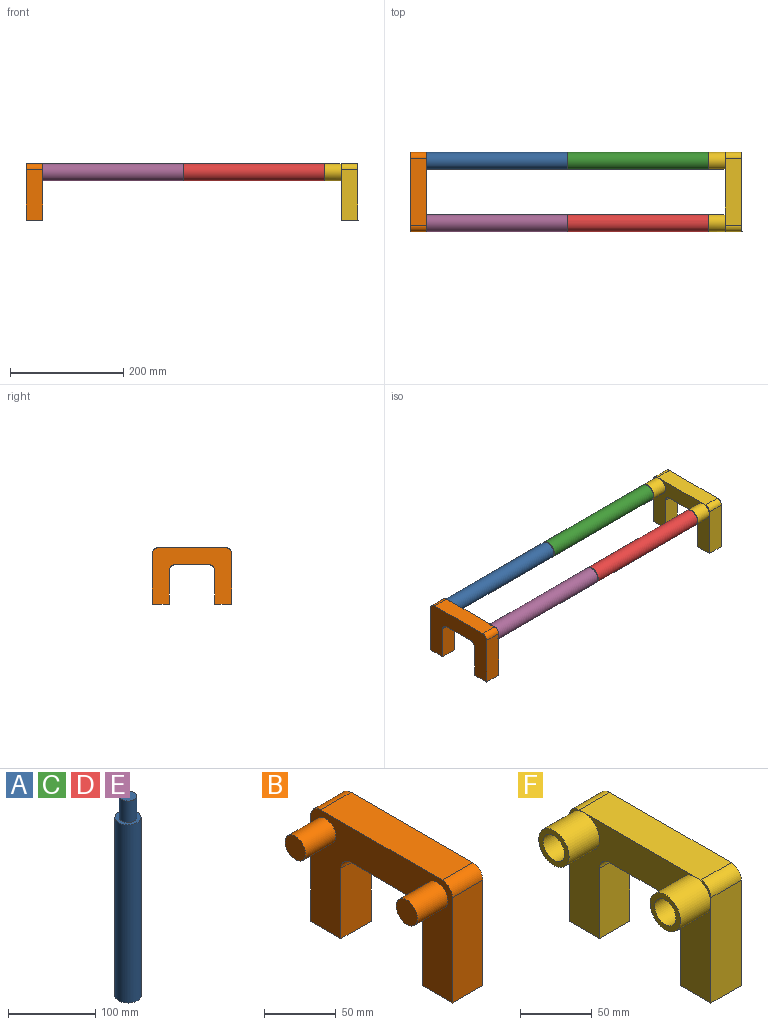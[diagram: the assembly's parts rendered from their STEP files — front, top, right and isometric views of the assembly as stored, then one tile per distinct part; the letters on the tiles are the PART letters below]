
ASSEMBLY  parts=6 mates=5
PART A: 7 faces, bbox 30x30x280 mm
  f0: cylinder r=15mm len=250mm, axis (0,0,-1), area 23561.9mm2, adj f1,f2
  f1: plane 30x30mm, normal (0,0,1), area 392.7mm2, adj f0,f3
  f2: plane 30x30mm, normal (0,0,-1), area 360.5mm2, adj f0,f5
  f3: cylinder r=10mm len=30mm, axis (0,0,-1), area 1885mm2, adj f1,f4
  f4: plane 20x20mm, normal (0,0,1), area 314.2mm2, adj f3
  f5: cylinder r=10.5mm len=31mm, axis (0,0,-1), area 2045.2mm2, adj f2,f6
  f6: plane 21x21mm, normal (0,0,-1), area 346.4mm2, adj f5
PART B: 18 faces, bbox 60x140x100 mm
  f0: plane 60x30mm, normal (0,1,0), area 1800mm2, adj f1,f3,f5,f16
  f1: plane 140x100mm, normal (-1,0,0), area 7739.5mm2, adj f0,f2,f4,f5,f6,f7,f8,f9
  f2: plane 90x30mm, normal (0,-1,0), area 2700mm2, adj f1,f3,f5,f15
  f3: plane 140x100mm, normal (1,0,0), area 8400mm2, adj f0,f2,f4,f5,f6,f7,f8,f9
  f4: plane 120x30mm, normal (0,0,1), area 3600mm2, adj f1,f3,f14,f15
  f5: plane 30x30mm, normal (0,0,-1), area 900mm2, adj f0,f1,f2,f3
  f6: plane 60x30mm, normal (0,-1,0), area 1800mm2, adj f1,f3,f8,f17
  f7: plane 90x30mm, normal (0,1,0), area 2700mm2, adj f1,f3,f8,f14
  f8: plane 30x30mm, normal (0,0,-1), area 900mm2, adj f1,f3,f6,f7
  f9: plane 60x30mm, normal (0,0,-1), area 1800mm2, adj f1,f3,f16,f17
  f10: cylinder r=10.5mm len=30mm, axis (1,0,0), area 1979.2mm2, adj f1,f11
  f11: plane 21x21mm, normal (-1,0,0), area 346.4mm2, adj f10
  f12: cylinder r=10mm len=30mm, axis (1,0,0), area 1885mm2, adj f1,f13
  f13: plane 20x20mm, normal (-1,0,0), area 314.2mm2, adj f12
  f14: cylinder r=10mm len=30mm, axis (1,0,0), area 471.2mm2, adj f1,f3,f4,f7
  f15: cylinder r=10mm len=30mm, axis (-1,0,0), area 471.2mm2, adj f1,f2,f3,f4
  f16: cylinder r=10mm len=30mm, axis (-1,0,0), area 471.2mm2, adj f0,f1,f3,f9
  f17: cylinder r=10mm len=30mm, axis (-1,0,0), area 471.2mm2, adj f1,f3,f6,f9
PART C: same geometry as A
PART D: same geometry as A
PART E: same geometry as A
PART F: 24 faces, bbox 60x140x100 mm
  f0: plane 15x15mm, normal (-1,0,0), area 26.8mm2, adj f5,f6,f15,f18
  f1: plane 140x100mm, normal (-1,0,0), area 6932.6mm2, adj f2,f5,f6,f7,f8,f9,f10,f11
  f2: plane 60x30mm, normal (0,-1,0), area 1800mm2, adj f1,f4,f7,f13
  f3: plane 15x15mm, normal (-1,0,0), area 26.8mm2, adj f6,f9,f14,f16
  f4: plane 140x100mm, normal (1,0,0), area 8400mm2, adj f2,f5,f6,f7,f8,f9,f10,f11
  f5: plane 90x30mm, normal (0,1,0), area 2700mm2, adj f0,f1,f4,f7,f15
  f6: plane 120x30mm, normal (0,0,1), area 3600mm2, adj f0,f1,f3,f4,f14,f15
  f7: plane 30x30mm, normal (0,0,-1), area 900mm2, adj f1,f2,f4,f5
  f8: plane 60x30mm, normal (0,1,0), area 1800mm2, adj f1,f4,f10,f12
  f9: plane 90x30mm, normal (0,-1,0), area 2700mm2, adj f1,f3,f4,f10,f14
  f10: plane 30x30mm, normal (0,0,-1), area 900mm2, adj f1,f4,f8,f9
  f11: plane 60x30mm, normal (0,0,-1), area 1800mm2, adj f1,f4,f12,f13
  f12: cylinder r=10mm len=30mm, axis (-1,0,0), area 471.2mm2, adj f1,f4,f8,f11
  f13: cylinder r=10mm len=30mm, axis (-1,0,0), area 471.2mm2, adj f1,f2,f4,f11
  f14: cylinder r=10mm len=30mm, axis (-1,0,0), area 471.2mm2, adj f3,f4,f6,f9
  f15: cylinder r=10mm len=30mm, axis (1,0,0), area 471.2mm2, adj f0,f4,f5,f6
  f16: cylinder r=15mm len=30mm, axis (1,0,0), area 2827.4mm2, adj f1,f3,f17
  f17: plane 30x30mm, normal (-1,0,0), area 360.5mm2, adj f16,f20
  f18: cylinder r=15mm len=30mm, axis (1,0,0), area 2827.4mm2, adj f0,f1,f19
  f19: plane 30x30mm, normal (-1,0,0), area 360.5mm2, adj f18,f22
  f20: cylinder r=10.5mm len=31mm, axis (-1,0,0), area 2045.2mm2, adj f17,f21
  f21: plane 21x21mm, normal (-1,0,0), area 346.4mm2, adj f20
  f22: cylinder r=10.5mm len=31mm, axis (-1,0,0), area 2045.2mm2, adj f19,f23
  f23: plane 21x21mm, normal (-1,0,0), area 346.4mm2, adj f22
PLACE A rot(axis=(-0.58,0.58,-0.58),120deg) t=(-363.22,232.21,144.62)mm
PLACE B rot(axis=(0,0,-1),180deg) t=(-362.22,177.21,59.62)mm
PLACE C rot(axis=(0.71,0,0.71),180deg) t=(-114.22,232.21,144.62)mm
PLACE D rot(axis=(0,1,0),90deg) t=(-114.22,122.21,144.62)mm
PLACE E rot(axis=(0.58,0.58,0.58),120deg) t=(-363.22,122.21,144.62)mm
PLACE F t=(164.78,177.21,59.62)mm
MATE fastened E.f3 <-> D.f5  axis (1,0,0) through (-83.22,122.21,144.62)mm
MATE fastened C.f3 <-> F.f18  axis (1,0,0) through (165.78,232.21,144.62)mm
MATE fastened A.f3 <-> C.f5  axis (1,0,0) through (-83.22,232.21,144.62)mm
MATE fastened B.f12 <-> E.f5  axis (1,0,0) through (-332.22,122.21,144.62)mm
MATE fastened D.f3 <-> F.f16  axis (1,0,0) through (165.78,122.21,144.62)mm
